# Revit family: 306_H6_X_-S2
name_source: partatom
category: Pipe Accessories
units: mm (PartAtom-declared; Revit-internal decimal feet)

## family parameters
Always vertical = Yes
Cut with Voids When Loaded = No
Part Type = Valve - Breaks Into
Round Connector Dimension = Use Diameter
Shared = No
Work Plane-Based = No

## types (16) — shared parameters
CAT0 = Yes
Description = Globe valve, 2-way, Flange, PN 25
L2D_Min = 3048 mm
Manufacturer = Belimo
QmdConnectorList = 301;D;302;D
magiPartTypeId = 306
magiProductFamilyId = H6*X*-S2
zero-valued in all types: MC_Default_elevation

## per-type parameters (varying)
| type | C | C__ve | CenSd_NR_6 | D | DD1 | DD2 | DR | FD | HH | HH1 | HH1__ve | HH2 | HH3 | HH4 | HH4__ve | HH5 | L2 | L2D | L4 | L42 | LL1 | LM | NR | W2D |
| H6015XP4-S2 | 14 mm  [stored 0.0459318 ft] | -14 mm  [stored -0.0459318 ft] | 13 mm | 15 mm | 38 mm  [stored 0.124672 ft] | 67 mm | 24 mm | 95 mm | 59 mm | 12 mm  [stored 0.0393701 ft] | -12 mm | 35 mm  [stored 0.114829 ft] | 47 mm | 38 mm  [stored 0.124672 ft] | -38 mm  [stored -0.124672 ft] | 24 mm | 65 mm | 130 mm | 33 mm | 26 mm | 43 mm | 102 mm | 15 mm  [stored 0.0492126 ft] | 15 mm  [stored 0.0492126 ft] |
| H6050X40-S2 | 20 mm  [stored 0.0656168 ft] | -20 mm  [stored -0.0656168 ft] | 26 mm | 50 mm | 66 mm | 116 mm | 41 mm | 165 mm | 70 mm | 14 mm  [stored 0.0459318 ft] | -14 mm  [stored -0.0459318 ft] | 42 mm  [stored 0.137795 ft] | 56 mm | 66 mm | -66 mm  [stored -0.216535 ft] | 28 mm | 115 mm | 230 mm | 58 mm | 45 mm  [stored 0.147638 ft] | 73 mm | 190 mm | 30 mm  [stored 0.0984252 ft] | 50 mm |
| H6050X25-S2 | 20 mm  [stored 0.0656168 ft] | -20 mm  [stored -0.0656168 ft] | 26 mm | 50 mm | 66 mm | 116 mm | 41 mm | 165 mm | 70 mm | 14 mm  [stored 0.0459318 ft] | -14 mm  [stored -0.0459318 ft] | 42 mm  [stored 0.137795 ft] | 56 mm | 66 mm | -66 mm  [stored -0.216535 ft] | 28 mm | 115 mm | 230 mm | 58 mm | 45 mm  [stored 0.147638 ft] | 73 mm | 190 mm | 30 mm  [stored 0.0984252 ft] | 50 mm |
| H6040X25-S2 | 18 mm  [stored 0.0590551 ft] | -18 mm  [stored -0.0590551 ft] | 26 mm | 40 mm | 60 mm | 105 mm | 38 mm  [stored 0.124672 ft] | 150 mm | 67 mm | 13 mm | -13 mm | 40 mm  [stored 0.131234 ft] | 53 mm | 60 mm | -60 mm  [stored -0.19685 ft] | 27 mm | 100 mm | 200 mm | 50 mm | 41 mm | 65 mm | 164 mm | 30 mm  [stored 0.0984252 ft] | 40 mm  [stored 0.131234 ft] |
| H6040X16-S2 | 18 mm  [stored 0.0590551 ft] | -18 mm  [stored -0.0590551 ft] | 26 mm | 40 mm | 60 mm | 105 mm | 38 mm  [stored 0.124672 ft] | 150 mm | 67 mm | 13 mm | -13 mm | 40 mm  [stored 0.131234 ft] | 53 mm | 60 mm | -60 mm  [stored -0.19685 ft] | 27 mm | 100 mm | 200 mm | 50 mm | 41 mm | 65 mm | 164 mm | 30 mm  [stored 0.0984252 ft] | 40 mm  [stored 0.131234 ft] |
| H6032X16-S2 | 18 mm  [stored 0.0590551 ft] | -18 mm  [stored -0.0590551 ft] | 13 mm | 32 mm | 56 mm | 98 mm | 35 mm  [stored 0.114829 ft] | 140 mm | 63 mm | 13 mm | -13 mm | 38 mm  [stored 0.124672 ft] | 50 mm | 56 mm | -56 mm  [stored -0.183727 ft] | 25 mm  [stored 0.082021 ft] | 90 mm | 180 mm | 45 mm  [stored 0.147638 ft] | 39 mm | 60 mm | 144 mm | 15 mm  [stored 0.0492126 ft] | 32 mm  [stored 0.104987 ft] |
| H6032X10-S2 | 18 mm  [stored 0.0590551 ft] | -18 mm  [stored -0.0590551 ft] | 13 mm | 32 mm | 56 mm | 98 mm | 35 mm  [stored 0.114829 ft] | 140 mm | 63 mm | 13 mm | -13 mm | 38 mm  [stored 0.124672 ft] | 50 mm | 56 mm | -56 mm  [stored -0.183727 ft] | 25 mm  [stored 0.082021 ft] | 90 mm | 180 mm | 45 mm  [stored 0.147638 ft] | 39 mm | 60 mm | 144 mm | 15 mm  [stored 0.0492126 ft] | 32 mm  [stored 0.104987 ft] |
| H6025X10-S2 | 16 mm  [stored 0.0524934 ft] | -16 mm  [stored -0.0524934 ft] | 13 mm | 25 mm | 46 mm  [stored 0.150919 ft] | 81 mm | 29 mm | 115 mm | 63 mm | 13 mm | -13 mm | 38 mm  [stored 0.124672 ft] | 50 mm | 46 mm  [stored 0.150919 ft] | -46 mm  [stored -0.150919 ft] | 25 mm  [stored 0.082021 ft] | 80 mm | 160 mm | 40 mm  [stored 0.131234 ft] | 32 mm  [stored 0.104987 ft] | 50 mm | 128 mm | 15 mm  [stored 0.0492126 ft] | 25 mm  [stored 0.082021 ft] |
| H6025X6P3-S2 | 16 mm  [stored 0.0524934 ft] | -16 mm  [stored -0.0524934 ft] | 13 mm | 25 mm | 46 mm  [stored 0.150919 ft] | 81 mm | 29 mm | 115 mm | 63 mm | 13 mm | -13 mm | 38 mm  [stored 0.124672 ft] | 50 mm | 46 mm  [stored 0.150919 ft] | -46 mm  [stored -0.150919 ft] | 25 mm  [stored 0.082021 ft] | 80 mm | 160 mm | 40 mm  [stored 0.131234 ft] | 32 mm  [stored 0.104987 ft] | 50 mm | 128 mm | 15 mm  [stored 0.0492126 ft] | 25 mm  [stored 0.082021 ft] |
| H6020X6P3-S2 | 16 mm  [stored 0.0524934 ft] | -16 mm  [stored -0.0524934 ft] | 13 mm | 20 mm | 42 mm  [stored 0.137795 ft] | 74 mm | 26 mm | 105 mm | 59 mm | 12 mm  [stored 0.0393701 ft] | -12 mm | 35 mm  [stored 0.114829 ft] | 47 mm | 42 mm  [stored 0.137795 ft] | -42 mm  [stored -0.137795 ft] | 24 mm | 75 mm | 150 mm | 38 mm  [stored 0.124672 ft] | 29 mm | 48 mm | 118 mm | 15 mm  [stored 0.0492126 ft] | 20 mm  [stored 0.0656168 ft] |
| H6020X4-S2 | 16 mm  [stored 0.0524934 ft] | -16 mm  [stored -0.0524934 ft] | 13 mm | 20 mm | 42 mm  [stored 0.137795 ft] | 74 mm | 26 mm | 105 mm | 59 mm | 12 mm  [stored 0.0393701 ft] | -12 mm | 35 mm  [stored 0.114829 ft] | 47 mm | 42 mm  [stored 0.137795 ft] | -42 mm  [stored -0.137795 ft] | 24 mm | 75 mm | 150 mm | 38 mm  [stored 0.124672 ft] | 29 mm | 48 mm | 118 mm | 15 mm  [stored 0.0492126 ft] | 20 mm  [stored 0.0656168 ft] |
| H6015X4-S2 | 14 mm  [stored 0.0459318 ft] | -14 mm  [stored -0.0459318 ft] | 13 mm | 15 mm | 38 mm  [stored 0.124672 ft] | 67 mm | 24 mm | 95 mm | 59 mm | 12 mm  [stored 0.0393701 ft] | -12 mm | 35 mm  [stored 0.114829 ft] | 47 mm | 38 mm  [stored 0.124672 ft] | -38 mm  [stored -0.124672 ft] | 24 mm | 65 mm | 130 mm | 33 mm | 26 mm | 43 mm | 102 mm | 15 mm  [stored 0.0492126 ft] | 15 mm  [stored 0.0492126 ft] |
| H6015X2P5-S2 | 14 mm  [stored 0.0459318 ft] | -14 mm  [stored -0.0459318 ft] | 13 mm | 15 mm | 38 mm  [stored 0.124672 ft] | 67 mm | 24 mm | 95 mm | 59 mm | 12 mm  [stored 0.0393701 ft] | -12 mm | 35 mm  [stored 0.114829 ft] | 47 mm | 38 mm  [stored 0.124672 ft] | -38 mm  [stored -0.124672 ft] | 24 mm | 65 mm | 130 mm | 33 mm | 26 mm | 43 mm | 102 mm | 15 mm  [stored 0.0492126 ft] | 15 mm  [stored 0.0492126 ft] |
| H6015X1P6-S2 | 14 mm  [stored 0.0459318 ft] | -14 mm  [stored -0.0459318 ft] | 13 mm | 15 mm | 38 mm  [stored 0.124672 ft] | 67 mm | 24 mm | 95 mm | 59 mm | 12 mm  [stored 0.0393701 ft] | -12 mm | 35 mm  [stored 0.114829 ft] | 47 mm | 38 mm  [stored 0.124672 ft] | -38 mm  [stored -0.124672 ft] | 24 mm | 65 mm | 130 mm | 33 mm | 26 mm | 43 mm | 102 mm | 15 mm  [stored 0.0492126 ft] | 15 mm  [stored 0.0492126 ft] |
| H6015X1-S2 | 14 mm  [stored 0.0459318 ft] | -14 mm  [stored -0.0459318 ft] | 13 mm | 15 mm | 38 mm  [stored 0.124672 ft] | 67 mm | 24 mm | 95 mm | 59 mm | 12 mm  [stored 0.0393701 ft] | -12 mm | 35 mm  [stored 0.114829 ft] | 47 mm | 38 mm  [stored 0.124672 ft] | -38 mm  [stored -0.124672 ft] | 24 mm | 65 mm | 130 mm | 33 mm | 26 mm | 43 mm | 102 mm | 15 mm  [stored 0.0492126 ft] | 15 mm  [stored 0.0492126 ft] |
| H6015XP63-S2 | 14 mm  [stored 0.0459318 ft] | -14 mm  [stored -0.0459318 ft] | 13 mm | 15 mm | 38 mm  [stored 0.124672 ft] | 67 mm | 24 mm | 95 mm | 59 mm | 12 mm  [stored 0.0393701 ft] | -12 mm | 35 mm  [stored 0.114829 ft] | 47 mm | 38 mm  [stored 0.124672 ft] | -38 mm  [stored -0.124672 ft] | 24 mm | 65 mm | 130 mm | 33 mm | 26 mm | 43 mm | 102 mm | 15 mm  [stored 0.0492126 ft] | 15 mm  [stored 0.0492126 ft] |

note: column(s) folded — value = type name in every type: magiProductCode, magiProductId

note: [stored X ft] marks values corroborated as IEEE doubles in the binary element streams (Revit-internal decimal feet)

## geometry (parser evidence)
native form markers: Sweep x1
no freeform markers — native parametric forms only
